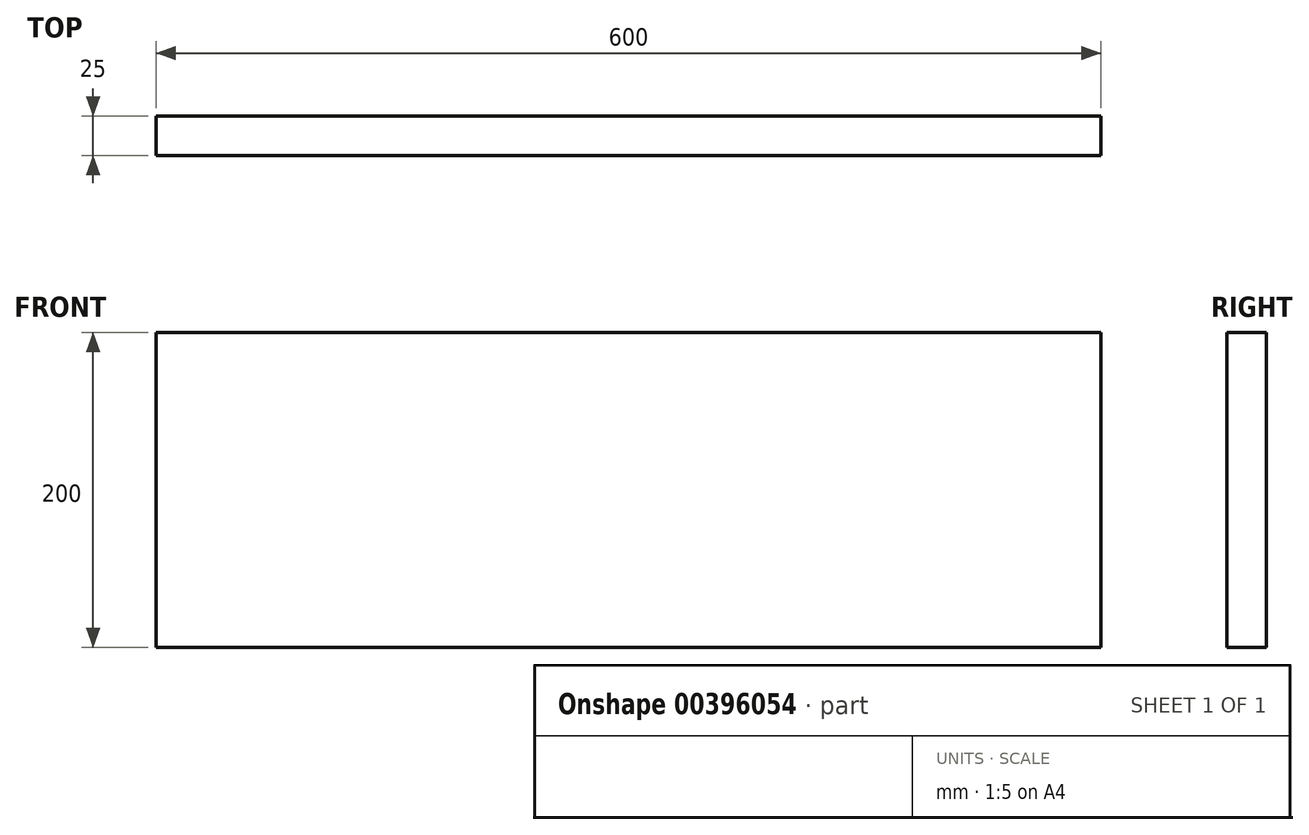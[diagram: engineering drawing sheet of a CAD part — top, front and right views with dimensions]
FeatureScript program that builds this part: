
annotation { "Feature Type Name" : "Feature", "Feature Type Description" : "" }
export const myFeature = defineFeature(function(context is Context, id is Id, definition is map)
    precondition{}
    {
        {
            var Q0;
            Q0=qCreatedBy(makeId("Front.planeOp"),FACE);
            var sketch = newSketch(context, id + "F0", { "sketchPlane" : qUnion([Q0])});
            skLineSegment(sketch, "E0.bottom", {"start": v(-300, 100) * mm, "end": v(300, 100) * mm});
            skLineSegment(sketch, "E0.top", {"start": v(-300, -100) * mm, "end": v(300, -100) * mm});
            skLineSegment(sketch, "E0.left", {"start": v(-300, 100) * mm, "end": v(-300, -100) * mm});
            skLineSegment(sketch, "E0.right", {"start": v(300, 100) * mm, "end": v(300, -100) * mm});
            skSolve(sketch);
        }
        {
            var Q0;
            Q0=makeQuery(id+"F0.imprint","IMPRINT",FACE,{"disambiguationData":[TD([[makeQuery(id+"F0.imprint","IMPRINT",EDGE,{"derivedFrom":sQuery(id+"F0.wireOp",EDGE,"E0.bottom")}),-1.0]])]});
            extrude(context, id + "F1", {"entities" : qUnion([Q0]), "depth" : 25 * mm});
        }
    });
